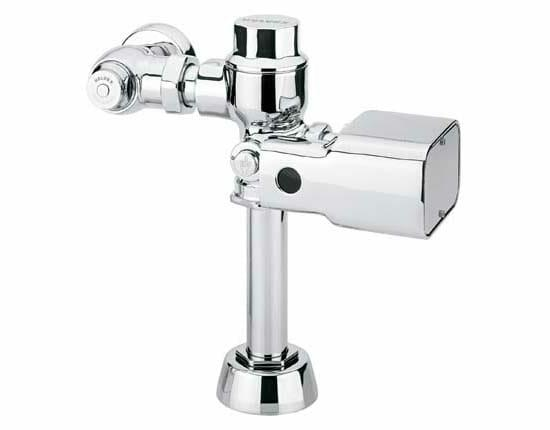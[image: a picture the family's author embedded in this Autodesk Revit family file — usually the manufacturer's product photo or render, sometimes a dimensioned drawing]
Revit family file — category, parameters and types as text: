
# Revit family: FB-110-38-3.5
name_source: partatom
category: Modelos genéricos
units: mm (PartAtom-declared; Revit-internal decimal feet)

## family parameters
Anfitrión = Cara
Compartido = Sí
Corte con vacíos al cargar = No
Cota de conector redondo = Diámetro de uso
Número OmniClass = 23.45.05.14.99
Puede alojar armadura = No
Punto de cálculo de habitación = Sí
Tipo de pieza = Normal
Título OmniClass = Other Sanitary Washing Plumbing Fixtures

## types (1)
- FB-110-38-3.5
    Comentarios de tipo = FLUXOMETRO PARA TAZA FLUX NAO O NAO17 DE SENSOR ELECTRONICO DE BATERIAS, SPUD DE 38 MM 3.5L POR DESCARGA
    Connection = 1"
    Descripción = FLUXOMETRO PARA TAZA FLUX NAO O NAO17 DE SENSOR ELECTRONICO DE BATERIAS, SPUD DE 38 MM 3.5L POR DESCARGA
    Elevación por defecto = 1 "
    Fabricante = HELVEX S.A. DE C.V.
    Imagen de tipo = FB-110-38-3.5.jpg
    Material = Brass Chromed
    Max. Working Pressure = 85.3 psi
    Min. Working Pressure = 14.2 psi
    Modelo = FB-110-38-3.5
    Note = La tubería de alimentación debe tener un Ø 32 mm mínimo y debe conectarse una reducción de campana de 32 mm - 25 mm a la llave de retención.
    URL = http://helvex.com.mx

## geometry (parser evidence)
native form markers: Sweep x5
no freeform markers — native parametric forms only
